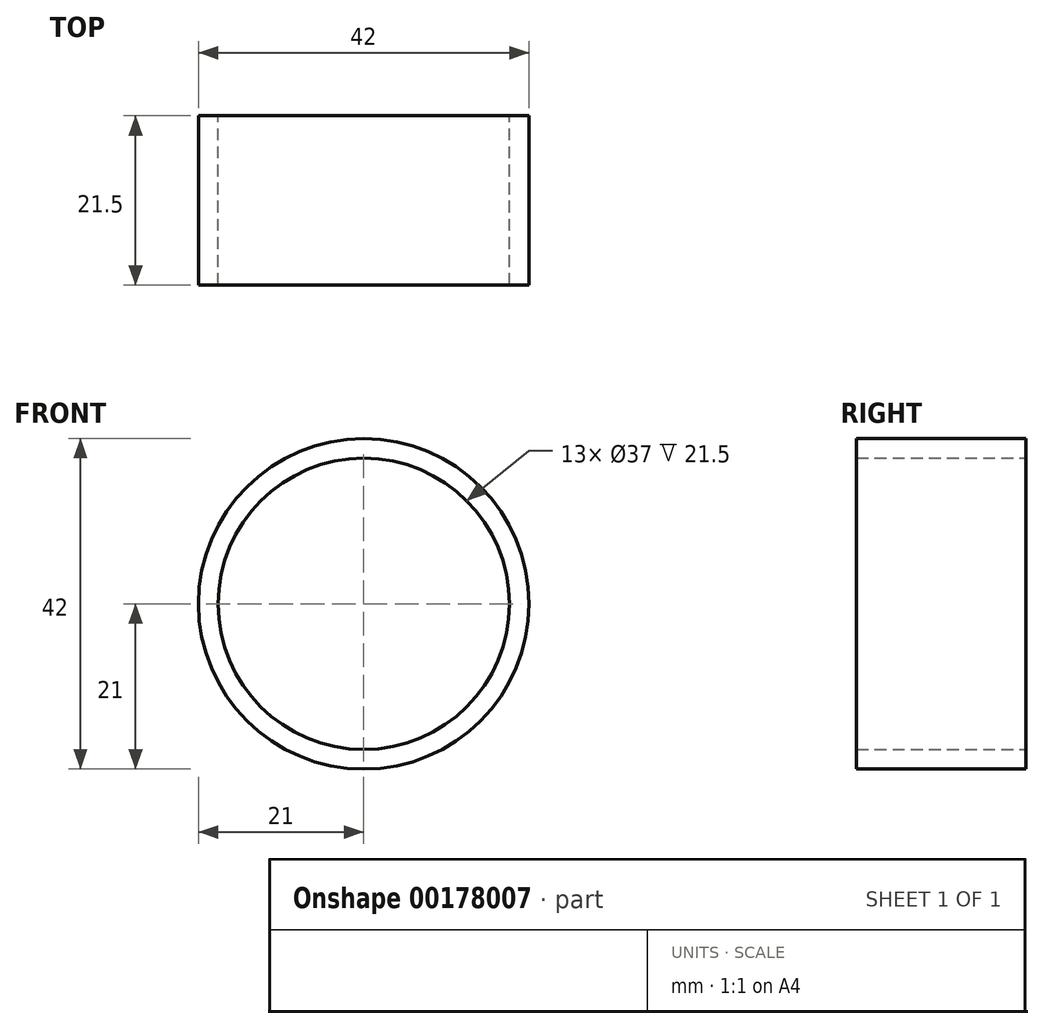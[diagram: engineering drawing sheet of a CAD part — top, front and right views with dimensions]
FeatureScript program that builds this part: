
annotation { "Feature Type Name" : "Feature", "Feature Type Description" : "" }
export const myFeature = defineFeature(function(context is Context, id is Id, definition is map)
    precondition{}
    {
        {
            var Q0;
            Q0=qCreatedBy(makeId("Front.planeOp"),FACE);
            var sketch = newSketch(context, id + "F0", { "sketchPlane" : qUnion([Q0])});
            skCircle(sketch, "E0", {"center": v(0, 0) * mm, "radius": 21 * mm});
            skCircle(sketch, "E1", {"center": v(0, 0) * mm, "radius": 18.5 * mm});
            skSolve(sketch);
        }
        {
            var Q0;
            Q0=qSketchRegion(id+"F0",true);
            extrude(context, id + "F1", {"entities" : qUnion([Q0]), "depth" : 10.75 * mm, "hasSecondDirection" : true, "secondDirectionOppositeDirection" : true, "secondDirectionDepth" : 10.75 * mm});
        }
    });
